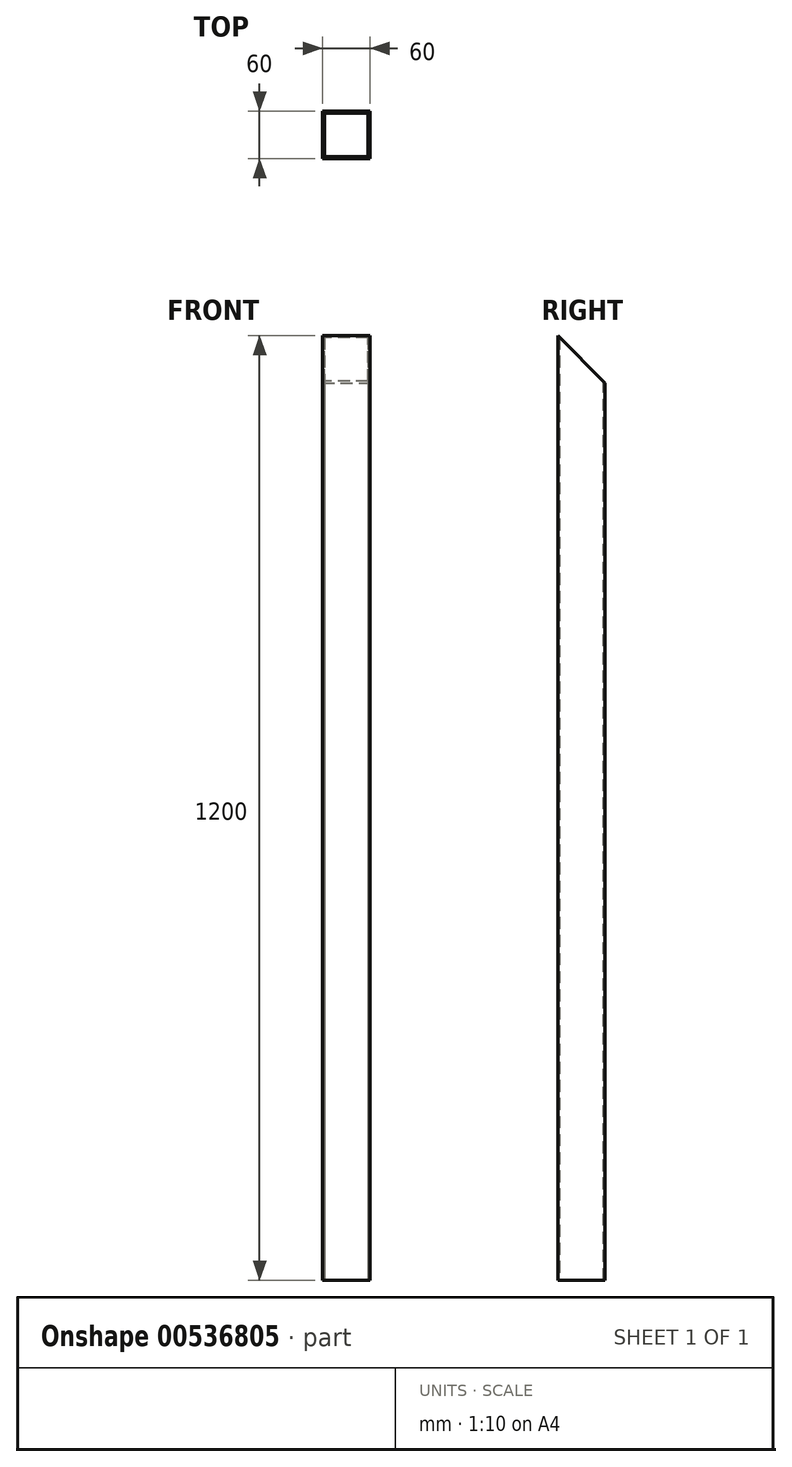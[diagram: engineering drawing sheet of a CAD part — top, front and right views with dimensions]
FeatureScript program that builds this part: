
annotation { "Feature Type Name" : "Feature", "Feature Type Description" : "" }
export const myFeature = defineFeature(function(context is Context, id is Id, definition is map)
    precondition{}
    {
        {
            var Q0;
            Q0=qCreatedBy(makeId("Top.planeOp"),FACE);
            var sketch = newSketch(context, id + "F0", { "sketchPlane" : qUnion([Q0])});
            skLineSegment(sketch, "E0.bottom", {"start": v(0, 0) * mm, "end": v(60, 0) * mm});
            skLineSegment(sketch, "E0.top", {"start": v(0, -60) * mm, "end": v(60, -60) * mm});
            skLineSegment(sketch, "E0.left", {"start": v(0, 0) * mm, "end": v(0, -60) * mm});
            skLineSegment(sketch, "E0.right", {"start": v(60, 0) * mm, "end": v(60, -60) * mm});
            skLineSegment(sketch, "E1.bottom", {"start": v(2.5, -57.5) * mm, "end": v(57.5, -57.5) * mm});
            skLineSegment(sketch, "E1.top", {"start": v(2.5, -2.5) * mm, "end": v(57.5, -2.5) * mm});
            skLineSegment(sketch, "E1.left", {"start": v(2.5, -57.5) * mm, "end": v(2.5, -2.5) * mm});
            skLineSegment(sketch, "E1.right", {"start": v(57.5, -57.5) * mm, "end": v(57.5, -2.5) * mm});
            skPoint(sketch, "E1.middle", {"position": v(30, -30) * mm});
            skPoint(sketch, "E1.middle.positionSnap0", {"position": v(60, -30) * mm});
            skPoint(sketch, "E1.middle.positionSnap1", {"position": v(30, -60) * mm});
            skPoint(sketch, "E1.centerSnap0", {"position": v(60, -30) * mm});
            skPoint(sketch, "E1.centerSnap1", {"position": v(30, -60) * mm});
            skSolve(sketch);
        }
        {
            var Q0;
            Q0=makeQuery(id+"F0.imprint","IMPRINT",FACE,{"disambiguationData":[TD([[makeQuery(id+"F0.imprint","IMPRINT",EDGE,{"derivedFrom":sQuery(id+"F0.wireOp",EDGE,"E0.bottom")}),-1.0]])]});
            extrude(context, id + "F1", {"entities" : qUnion([Q0]), "depth" : 1200 * mm, "offsetDistance" : 25 * mm});
        }
        {
            var Q0;
            Q0=makeQuery(id+"F1.opExtrude","SWEPT_FACE",FACE,{"disambiguationData":[OSD([sQuery(id+"F0.wireOp",EDGE,"E0.right")])]});
            var sketch = newSketch(context, id + "F2", { "sketchPlane" : qUnion([Q0])});
            skLineSegment(sketch, "E2", {"start": v(-60, 1200) * mm, "end": v(0, 1140) * mm});
            skSolve(sketch);
        }
        {
            var Q0;
            {var subQ0=sQuery(id+"F2.wireOp",EDGE,"E2");Q0=makeQuery(id+"F2.imprint","IMPRINT",FACE,{"disambiguationData":[TD([[makeQuery(id+"F2.imprint","IMPRINT",EDGE,{"derivedFrom":subQ0}),1.0]])]});}
            extrude(context, id + "F3", {"entities" : qUnion([Q0]), "operationType" : NewBodyOperationType.REMOVE, "oppositeDirection" : true, "depth" : 70 * mm, "offsetDistance" : 25 * mm});
        }
    });
